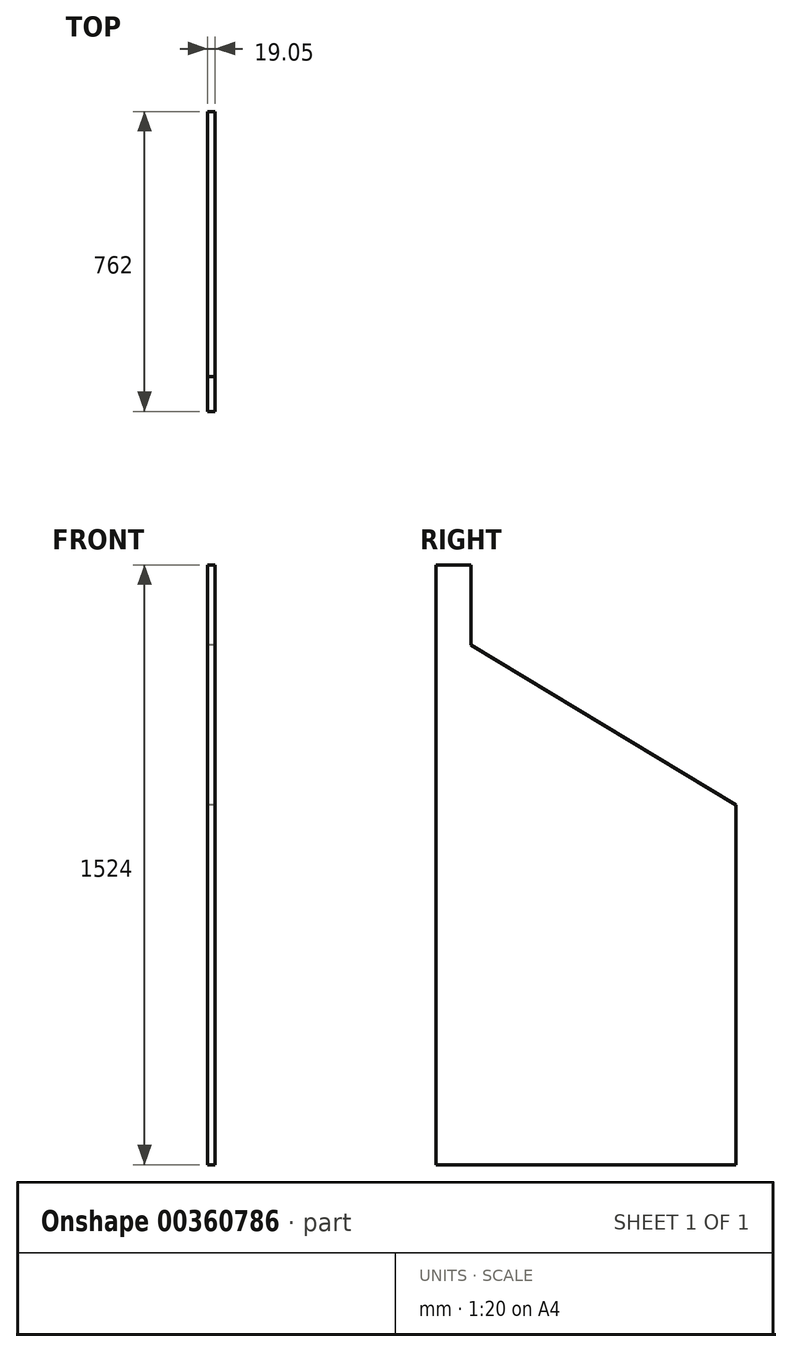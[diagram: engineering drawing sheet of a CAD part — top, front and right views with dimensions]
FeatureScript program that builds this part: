
annotation { "Feature Type Name" : "Feature", "Feature Type Description" : "" }
export const myFeature = defineFeature(function(context is Context, id is Id, definition is map)
    precondition{}
    {
        {
            var Q0;
            Q0=qCreatedBy(makeId("Right.planeOp"),FACE);
            var sketch = newSketch(context, id + "F0", { "sketchPlane" : qUnion([Q0])});
            skLineSegment(sketch, "E0", {"start": v(0, 0) * mm, "end": v(0, 1524) * mm});
            skLineSegment(sketch, "E1", {"start": v(0, 0) * mm, "end": v(762, 0) * mm});
            skLineSegment(sketch, "E2", {"start": v(0, 1524) * mm, "end": v(88.44, 1524) * mm});
            skLineSegment(sketch, "E3", {"start": v(88.44, 1524) * mm, "end": v(88.44, 1524) * mm});
            skLineSegment(sketch, "E4", {"start": v(88.44, 1320.8) * mm, "end": v(88.44, 1524) * mm});
            skLineSegment(sketch, "E5", {"start": v(762, 914.4) * mm, "end": v(762, 0) * mm});
            skLineSegment(sketch, "E6", {"start": v(762, 914.4) * mm, "end": v(88.44, 1320.8) * mm});
            skSolve(sketch);
        }
        {
            var Q0;
            Q0=makeQuery(id+"F0.imprint","IMPRINT",FACE,{"disambiguationData":[TD([[makeQuery(id+"F0.imprint","IMPRINT",EDGE,{"derivedFrom":sQuery(id+"F0.wireOp",EDGE,"E0")}),-1.0]])]});
            extrude(context, id + "F1", {"entities" : qUnion([Q0]), "depth" : 19.05 * mm});
        }
    });
